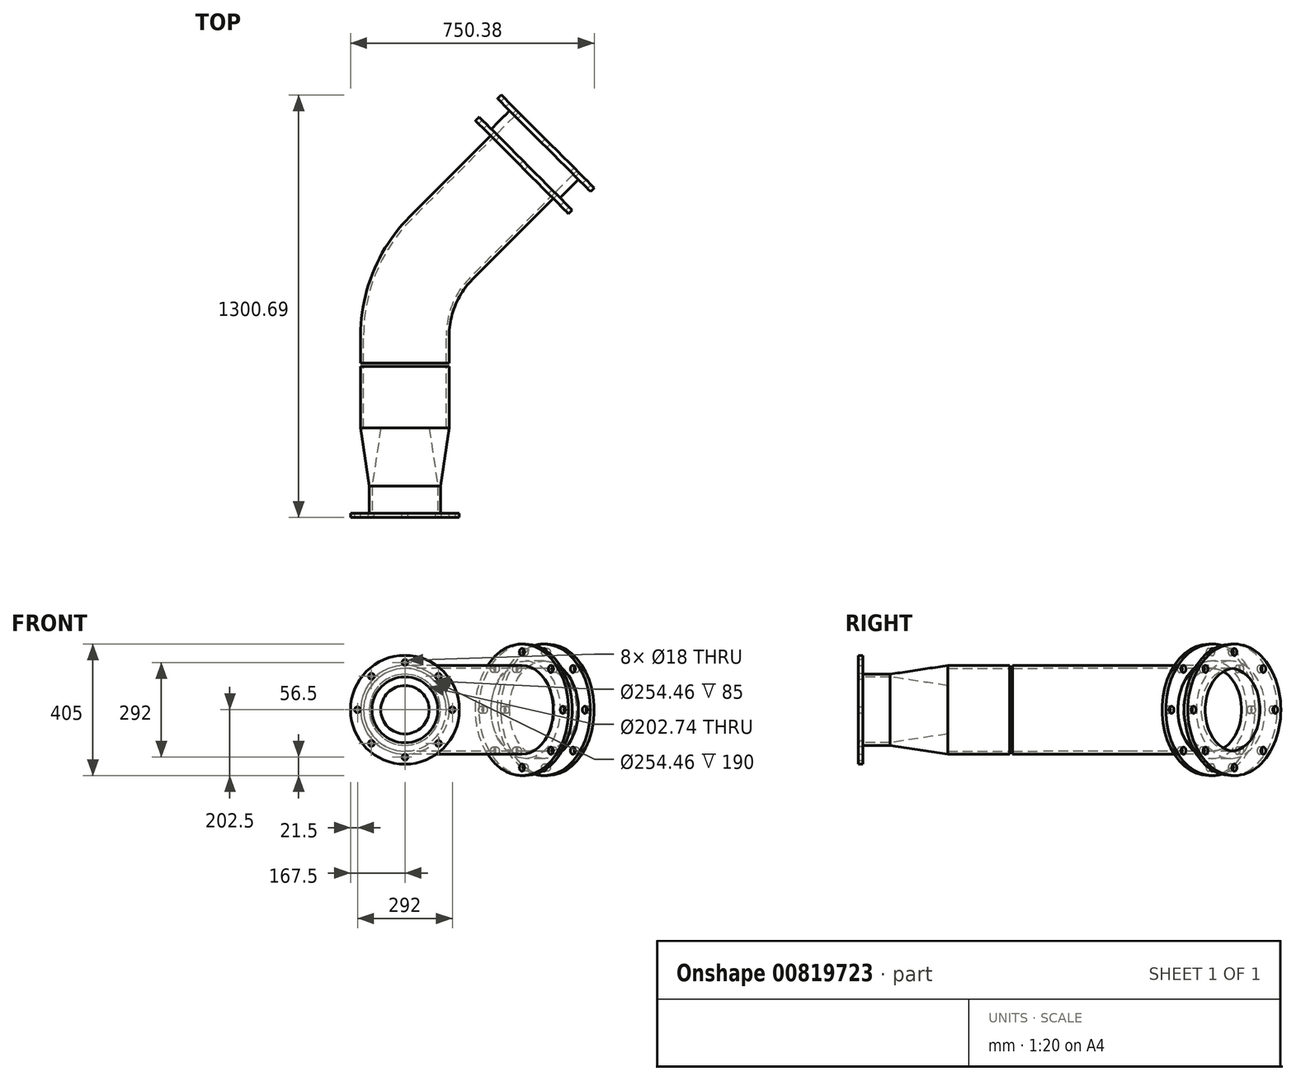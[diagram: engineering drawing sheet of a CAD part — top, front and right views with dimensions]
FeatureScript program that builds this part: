
annotation { "Feature Type Name" : "Feature", "Feature Type Description" : "" }
export const myFeature = defineFeature(function(context is Context, id is Id, definition is map)
    precondition{}
    {
        {
            var Q0;
            Q0=qCreatedBy(makeId("Front.planeOp"),FACE);
            var sketch = newSketch(context, id + "F0", { "sketchPlane" : qUnion([Q0])});
            skCircle(sketch, "E0", {"center": v(-381, 0) * mm, "radius": 136.5 * mm});
            skCircle(sketch, "E1", {"center": v(-381, 0) * mm, "radius": 127.23 * mm});
            skSolve(sketch);
        }
        {
            var Q0;
            Q0=qCreatedBy(makeId("Right.planeOp"),FACE);
            var sketch = newSketch(context, id + "F1", { "sketchPlane" : qUnion([Q0])});
            skLineSegment(sketch, "E2", {"start": v(0, 139.88) * mm, "end": v(0, -207.7) * mm, "construction": true});
            skSolve(sketch);
        }
        {
            var Q0;
            Q0 = qSketchRegion(id + "F0", true);
            var Q1;
            Q1=sQuery(id+"F1.wireOp",EDGE,"E2");
            revolve(context, id + "F2", {"surfaceOperationType" : NewSurfaceOperationType.NEW, "entities" : qUnion([Q0]), "axis" : qUnion([Q1]), "revolveType" : RevolveType.ONE_DIRECTION, "angle" : 45 * degree});
        }
        {
            var Q0;
            Q0=makeQuery(id+"F2.opRevolve","CAP_FACE",FACE,{"disambiguationData":[OSD([sQuery(id+"F0.wireOp",EDGE,"E0"),sQuery(id+"F0.wireOp",EDGE,"E1")])],"isStart":true});
            var sketch = newSketch(context, id + "F3", { "sketchPlane" : qUnion([Q0])});
            skCircle(sketch, "E3", {"center": v(-381, 0) * mm, "radius": 136.5 * mm});
            skCircle(sketch, "E4", {"center": v(-381, 0) * mm, "radius": 127.23 * mm});
            skSolve(sketch);
        }
        {
            var Q0;
            Q0 = qSketchRegion(id + "F3", true);
            extrude(context, id + "F4", {"entities" : qUnion([Q0]), "operationType" : NewBodyOperationType.ADD, "depth" : 85 * mm, "offsetDistance" : 25 * mm});
        }
        {
            var Q0;
            Q0=makeQuery(id+"F4.opExtrude","CAP_FACE",FACE,{"disambiguationData":[OSD([sQuery(id+"F3.wireOp",EDGE,"E3"),sQuery(id+"F3.wireOp",EDGE,"E4")])],"isStart":false});
            var sketch = newSketch(context, id + "F5", { "sketchPlane" : qUnion([Q0])});
            skCircle(sketch, "E5", {"center": v(-381, 0) * mm, "radius": 136.5 * mm});
            skCircle(sketch, "E6", {"center": v(-381, 0) * mm, "radius": 127.23 * mm});
            skSolve(sketch);
        }
        {
            var Q0;
            Q0 = qSketchRegion(id + "F5", true);
            var Q1;
            Q1 = qConstructionFilter(qBodyType(qCreatedBy(id + "F5" ,EDGE), BodyType.WIRE), ConstructionObject.NO);
            extrude(context, id + "F6", {"entities" : qUnion([Q0]), "surfaceEntities" : qUnion([Q1]), "depth" : 200 * mm, "offsetDistance" : 25 * mm, "hasSecondDirection" : true, "secondDirectionOppositeDirection" : false, "secondDirectionDepth" : 10 * mm});
        }
        {
            var Q0;
            Q0=makeQuery(id+"F6.opExtrude","CAP_FACE",FACE,{"disambiguationData":[OSD([sQuery(id+"F5.wireOp",EDGE,"E5"),sQuery(id+"F5.wireOp",EDGE,"E6")])],"isStart":false});
            cPlane(context, id + "F7", {"entities" : qUnion([Q0]), "cplaneType" : CPlaneType.OFFSET, "offset" : 178 * mm, "width" : 150 * mm, "height" : 150 * mm});
        }
        {
            var Q0;
            Q0=qCreatedBy(id+"F7.planeOp",FACE);
            var sketch = newSketch(context, id + "F8", { "sketchPlane" : qUnion([Q0])});
            skCircle(sketch, "E7", {"center": v(-381, 0) * mm, "radius": 109.55 * mm});
            skCircle(sketch, "E8", {"center": v(-381, 0) * mm, "radius": 101.37 * mm});
            skSolve(sketch);
        }
        {
            var Q0;
            Q0 = qSketchRegion(id + "F8", true);
            extrude(context, id + "F9", {"entities" : qUnion([Q0]), "oppositeDirection" : true, "depth" : 178 * mm, "offsetDistance" : 25 * mm, "hasDraft" : true, "draftAngle" : 8.6 * degree, "hasSecondDirection" : true, "secondDirectionOppositeDirection" : false, "secondDirectionDepth" : 84 * mm});
        }
        {
            var Q0;
            Q0=makeQuery(id+"F2.opRevolve","CAP_FACE",FACE,{"disambiguationData":[OSD([sQuery(id+"F0.wireOp",EDGE,"E0"),sQuery(id+"F0.wireOp",EDGE,"E1")])],"isStart":false});
            var sketch = newSketch(context, id + "F10", { "sketchPlane" : qUnion([Q0])});
            skCircle(sketch, "E9", {"center": v(381, 0) * mm, "radius": 136.5 * mm});
            skCircle(sketch, "E10", {"center": v(381, 0) * mm, "radius": 127.23 * mm});
            skSolve(sketch);
        }
        {
            var Q0;
            Q0 = qSketchRegion(id + "F10", true);
            extrude(context, id + "F11", {"entities" : qUnion([Q0]), "operationType" : NewBodyOperationType.ADD, "depth" : 352 * mm, "offsetDistance" : 25 * mm});
        }
        {
            var Q0;
            Q0=makeQuery(id+"F11.opExtrude","CAP_FACE",FACE,{"disambiguationData":[OSD([sQuery(id+"F10.wireOp",EDGE,"E9"),sQuery(id+"F10.wireOp",EDGE,"E10")])],"isStart":false});
            var sketch = newSketch(context, id + "F12", { "sketchPlane" : qUnion([Q0])});
            skCircle(sketch, "E11", {"center": v(381, 0) * mm, "radius": 127.23 * mm});
            skCircle(sketch, "E12", {"center": v(381, 0) * mm, "radius": 202.5 * mm});
            skCircle(sketch, "E13", {"center": v(381, 0) * mm, "radius": 178 * mm, "construction": true});
            skCircle(sketch, "E14", {"center": v(559, 0) * mm, "radius": 11 * mm});
            skCircle(sketch, "E15.1.0", {"center": v(506.87, 125.87) * mm, "radius": 11 * mm});
            skCircle(sketch, "E15.2.0", {"center": v(381, 178) * mm, "radius": 11 * mm});
            skCircle(sketch, "E15.3.0", {"center": v(255.13, 125.87) * mm, "radius": 11 * mm});
            skCircle(sketch, "E15.4.0", {"center": v(203, 0) * mm, "radius": 11 * mm});
            skCircle(sketch, "E15.5.0", {"center": v(255.13, -125.87) * mm, "radius": 11 * mm});
            skCircle(sketch, "E15.6.0", {"center": v(381, -178) * mm, "radius": 11 * mm});
            skCircle(sketch, "E15.7.0", {"center": v(506.87, -125.87) * mm, "radius": 11 * mm});
            skSolve(sketch);
        }
        {
            var Q0;
            Q0 = qSketchRegion(id + "F12", true);
            extrude(context, id + "F13", {"entities" : qUnion([Q0]), "operationType" : NewBodyOperationType.ADD, "depth" : 16 * mm, "offsetDistance" : 25 * mm});
        }
        {
            var Q0;
            Q0=makeQuery(id+"F13.opExtrude","CAP_FACE",FACE,{"disambiguationData":[OSD([sQuery(id+"F12.wireOp",EDGE,"E11"),sQuery(id+"F12.wireOp",EDGE,"E12"),sQuery(id+"F12.wireOp",EDGE,"E14"),sQuery(id+"F12.wireOp",EDGE,"E15.1.0"),sQuery(id+"F12.wireOp",EDGE,"E15.2.0"),sQuery(id+"F12.wireOp",EDGE,"E15.3.0"),sQuery(id+"F12.wireOp",EDGE,"E15.4.0"),sQuery(id+"F12.wireOp",EDGE,"E15.5.0"),sQuery(id+"F12.wireOp",EDGE,"E15.6.0"),sQuery(id+"F12.wireOp",EDGE,"E15.7.0")])],"isStart":false});
            var sketch = newSketch(context, id + "F14", { "sketchPlane" : qUnion([Q0])});
            skCircle(sketch, "E16", {"center": v(381, 0) * mm, "radius": 127.23 * mm});
            skCircle(sketch, "E17", {"center": v(381, 0) * mm, "radius": 150 * mm});
            skSolve(sketch);
        }
        {
            var Q0;
            Q0 = qSketchRegion(id + "F14", true);
            extrude(context, id + "F15", {"entities" : qUnion([Q0]), "depth" : 80 * mm, "offsetDistance" : 25 * mm});
        }
        {
            var Q0;
            Q0=makeQuery(id+"F15.opExtrude","CAP_FACE",FACE,{"disambiguationData":[OSD([sQuery(id+"F14.wireOp",EDGE,"E16"),sQuery(id+"F14.wireOp",EDGE,"E17")])],"isStart":false});
            var sketch = newSketch(context, id + "F16", { "sketchPlane" : qUnion([Q0])});
            skCircle(sketch, "E18", {"center": v(381, 0) * mm, "radius": 127.23 * mm});
            skCircle(sketch, "E19", {"center": v(381, 0) * mm, "radius": 202.5 * mm});
            skCircle(sketch, "E20", {"center": v(381, 0) * mm, "radius": 178 * mm, "construction": true});
            skCircle(sketch, "E21", {"center": v(559, 0) * mm, "radius": 11 * mm});
            skPoint(sketch, "E22.center", {"position": v(85.45, -110.74) * mm});
            skCircle(sketch, "E23.1.0", {"center": v(506.87, 125.87) * mm, "radius": 11 * mm});
            skCircle(sketch, "E23.2.0", {"center": v(381, 178) * mm, "radius": 11 * mm});
            skCircle(sketch, "E23.3.0", {"center": v(255.13, 125.87) * mm, "radius": 11 * mm});
            skCircle(sketch, "E23.4.0", {"center": v(203, 0) * mm, "radius": 11 * mm});
            skCircle(sketch, "E23.5.0", {"center": v(255.13, -125.87) * mm, "radius": 11 * mm});
            skCircle(sketch, "E23.6.0", {"center": v(381, -178) * mm, "radius": 11 * mm});
            skCircle(sketch, "E23.7.0", {"center": v(506.87, -125.87) * mm, "radius": 11 * mm});
            skLineSegment(sketch, "E24", {"start": v(381, 0) * mm, "end": v(469.4, 0) * mm, "construction": true});
            skSolve(sketch);
        }
        {
            var Q0;
            Q0 = qSketchRegion(id + "F16", true);
            extrude(context, id + "F17", {"entities" : qUnion([Q0]), "depth" : 16 * mm, "offsetDistance" : 25 * mm});
        }
        {
            var Q0;
            Q0=makeQuery(id+"F9.opExtrude","CAP_FACE",FACE,{"disambiguationData":[OSD([sQuery(id+"F8.wireOp",EDGE,"E7"),sQuery(id+"F8.wireOp",EDGE,"E8")])],"isStart":true});
            var sketch = newSketch(context, id + "F18", { "sketchPlane" : qUnion([Q0])});
            skCircle(sketch, "E25", {"center": v(-381, 0) * mm, "radius": 101.37 * mm});
            skCircle(sketch, "E26", {"center": v(-381, 0) * mm, "radius": 167.5 * mm});
            skCircle(sketch, "E27", {"center": v(-381, 0) * mm, "radius": 146 * mm, "construction": true});
            skCircle(sketch, "E28", {"center": v(-527, 0) * mm, "radius": 9 * mm});
            skCircle(sketch, "E29.1.0", {"center": v(-484.24, -103.24) * mm, "radius": 9 * mm});
            skCircle(sketch, "E29.2.0", {"center": v(-381, -146) * mm, "radius": 9 * mm});
            skCircle(sketch, "E29.3.0", {"center": v(-277.76, -103.24) * mm, "radius": 9 * mm});
            skCircle(sketch, "E29.4.0", {"center": v(-235, 0) * mm, "radius": 9 * mm});
            skCircle(sketch, "E29.5.0", {"center": v(-277.76, 103.24) * mm, "radius": 9 * mm});
            skCircle(sketch, "E29.6.0", {"center": v(-381, 146) * mm, "radius": 9 * mm});
            skCircle(sketch, "E29.7.0", {"center": v(-484.24, 103.24) * mm, "radius": 9 * mm});
            skSolve(sketch);
        }
        {
            var Q0;
            Q0 = qSketchRegion(id + "F18", true);
            extrude(context, id + "F19", {"entities" : qUnion([Q0]), "operationType" : NewBodyOperationType.ADD, "depth" : 13 * mm, "offsetDistance" : 25 * mm});
        }
    });
